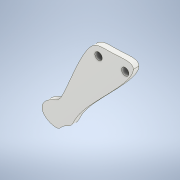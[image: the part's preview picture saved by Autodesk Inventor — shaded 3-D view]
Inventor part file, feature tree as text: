
AUTODESK INVENTOR PART (.ipt)
format: ipt  version: 2022 (Build 260153000, 153)  size: 124,928 bytes
history: native  units: in
note: dims shown in document units (in); Inventor stores cm internally (conversion verified against a paired STEP export)
features: extrude x1, sketch x1
ambient origin geometry x8: Origin, YZ Plane, XZ Plane, XY Plane, X Axis, Y Axis, Z Axis, Center Point
bodies: Solid1 (feature_tree)
feature tree (2):
  extrude  "Extrusion1"  Depth=0.2559in
  sketch  "Sketch2"  dims[d0=0.1969in d1=0.0in d2=0.2559in]
